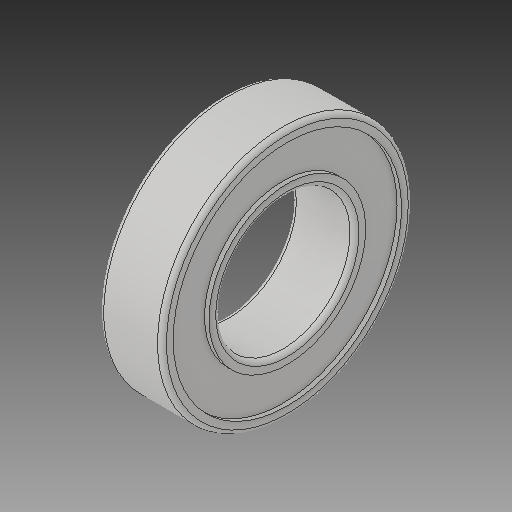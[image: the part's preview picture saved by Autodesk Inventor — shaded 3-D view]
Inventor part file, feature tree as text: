
AUTODESK INVENTOR PART (.ipt)
format: ipt  version: 2018 (Build 220112000, 112)  size: 177,152 bytes
history: native  units: in
note: dims shown in document units (in); Inventor stores cm internally (conversion verified against a paired STEP export)
features: fillet x1
ambient origin geometry x8: Origin, YZ Plane, XZ Plane, XY Plane, X Axis, Y Axis, Z Axis, Center Point
bodies: Solid1 (feature_tree)
feature tree (1):
  fillet  "Fillet1"  [1 undecoded]
note: 1 required parameter value undecoded (feature->parameter linkage not recoverable at this tier; creation-order binding heuristic only, values carry confidence <= 0.55)
